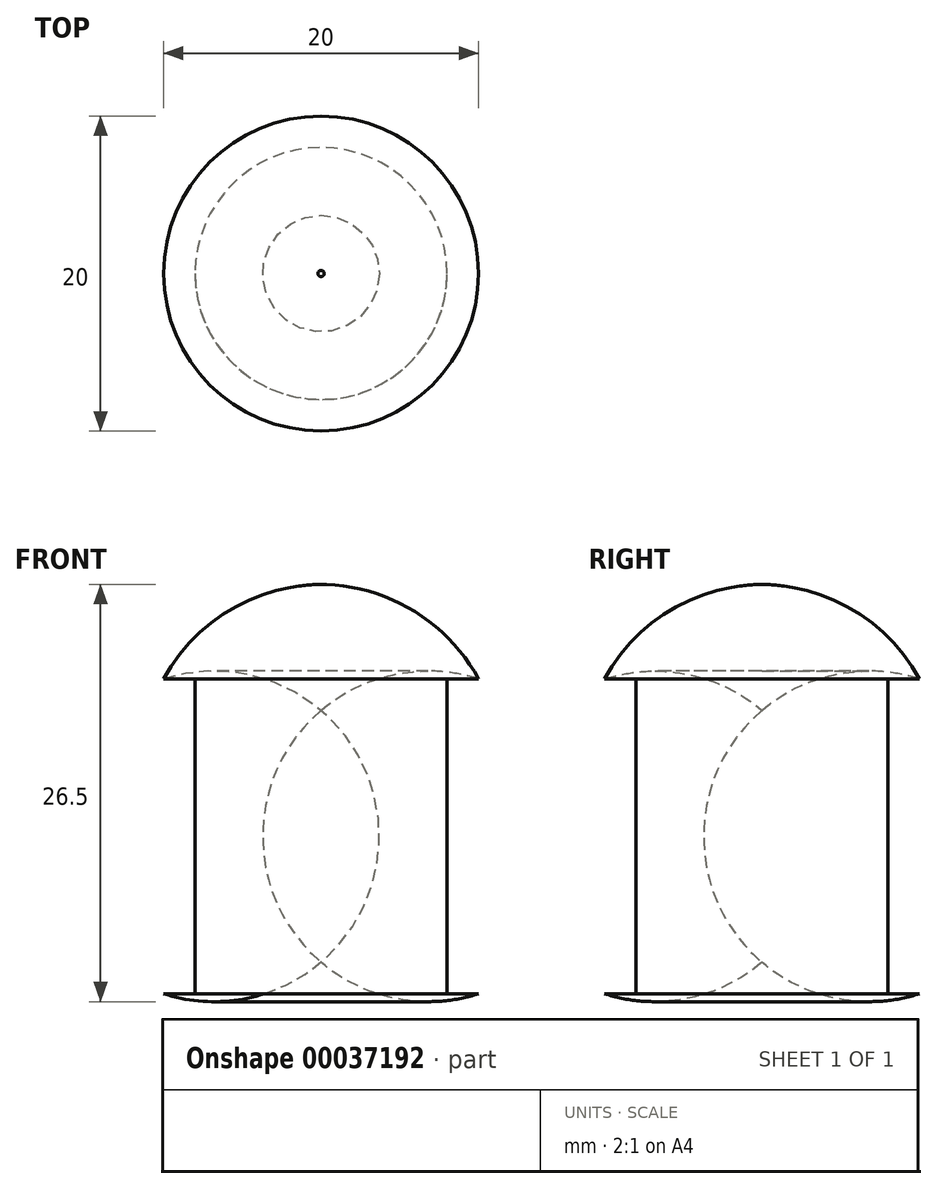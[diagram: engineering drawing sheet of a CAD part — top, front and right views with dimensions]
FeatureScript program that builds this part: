
annotation { "Feature Type Name" : "Feature", "Feature Type Description" : "" }
export const myFeature = defineFeature(function(context is Context, id is Id, definition is map)
    precondition{}
    {
        {
            var Q0;
            Q0=qCreatedBy(makeId("Top.planeOp"),FACE);
            var sketch = newSketch(context, id + "F0", { "sketchPlane" : qUnion([Q0])});
            skCircle(sketch, "E0", {"center": v(0, 0) * mm, "radius": 8 * mm});
            skCircle(sketch, "E1", {"center": v(0, 0) * mm, "radius": 10 * mm});
            skLineSegment(sketch, "E2", {"start": v(8, 0) * mm, "end": v(10, 0) * mm, "construction": true});
            skSolve(sketch);
        }
        {
            var Q0;
            Q0 = qSketchRegion(id + "F0", true);
            extrude(context, id + "F1", {"entities" : qUnion([Q0]), "depth" : 20 * mm});
        }
        {
            var Q0;
            Q0=qCreatedBy(makeId("Front.planeOp"),FACE);
            var sketch = newSketch(context, id + "F2", { "sketchPlane" : qUnion([Q0])});
            skLineSegment(sketch, "E3", {"start": v(10, 20) * mm, "end": v(10, 0) * mm});
            skLineSegment(sketch, "E4", {"start": v(0, 0) * mm, "end": v(10, 0) * mm, "construction": true});
            skArc(sketch, "E5", {"start": v(10, 0) * mm, "mid": v(17.3, 10) * mm, "end": v(10, 20) * mm});
            skLineSegment(sketch, "E6", {"start": v(0, 0) * mm, "end": v(0, 20) * mm, "construction": true});
            skLineSegment(sketch, "E7", {"start": v(0, 20) * mm, "end": v(0, 26) * mm});
            skLineSegment(sketch, "E8", {"start": v(0, 20) * mm, "end": v(10, 20) * mm});
            skArc(sketch, "E9", {"start": v(10, 20) * mm, "mid": v(5.82, 24.36) * mm, "end": v(0, 26) * mm});
            skSolve(sketch);
        }
        {
            var Q0;
            Q0 = qSketchRegion(id + "F2", true);
            var Q1;
            Q1=sQuery(id+"F2.wireOp",EDGE,"E6");
            revolve(context, id + "F3", {"operationType" : NewBodyOperationType.ADD, "entities" : qUnion([Q0]), "axis" : qUnion([Q1]), "revolveType" : RevolveType.FULL});
        }
    });
